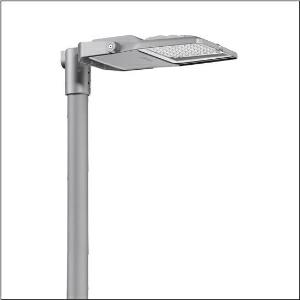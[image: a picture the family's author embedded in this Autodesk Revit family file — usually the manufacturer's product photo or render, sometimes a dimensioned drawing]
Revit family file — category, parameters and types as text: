
# Revit family: floodlight_fl_21_mini___pl52_5xa7776c4d3a_f656
name_source: partatom
category: Lighting Fixtures
units: mm (PartAtom-declared; Revit-internal decimal feet)

## family parameters
Cut with Voids When Loaded = No
Host = Face
Light Source = No
Part Type = Normal
Room Calculation Point = No
Round Connector Dimension = Use Diameter
Shared = No

## types (1)
- --- (1 x LED, 12700 lm, 89 W, 4000K)
    Apparent Load = 89 VA
    CIE Flux Codes = 26 60 98 100 100
    Color Rendering = 70
    Color Temperature = 4000K
    Default Elevation = 1800 mm
    Description = Floodlight FL 21 mini, floodlight, primary light control with lens, of PMMA, primary optical cover: protective disc, of toughened safety glass, transparent, light distribution: PL52, light emission: direct distribution, installation type: surface-mounted, LED, High Power LED, rated luminous flux: 12.700lm, luminous efficacy: 143lm/W, light colour: 740, colour temperature: 4000K, control gear: Smart Interface (Zhaga), control: pre-setting: logarithmic dimming characteristic, flexible luminous flux parameterisation, time-dependent luminous flux control, constant luminous flux control, overheat protection, with terminal, 6-pole, mains connection: 220..240V, AC, 50/60Hz, start of lifetime: 89W, end of service life: 94W, reduction: 43W, luminaire housing, of diecast aluminium, powder-coated, SITECO metallic grey (DB 702S), corrosivity category C5 mid according to DIN EN ISO 12944, suitable for swimming pools, chlorine-resistant, sealing non-destructively replaceable, please order mast flange separately, mast bracket, of steel, galvanised, powder-coated, SITECO metallic grey (DB 702S), Smart Interface below and above, protection rating (complete): IP66, insulation class (complete): insulation class II (safety insulation), certification: CE, ENEC, VDE, protection symbol: D, impact resistance: IK08, permissible operating ambient temperature: -40..+40°C, permissible operating ambient temperature for outdoor applications: -40..+50°C, standard: DIN EN 12944, LABS conformity tested according to VDMA 24364:2018-05, packaging unit: 1 piece

Light Distribution: PL52
    Height = 70 mm
    Lamp = 1 x LED
    Lamp Light Flux = 12700 lm
    Lamp Power = 89 W
    Lamp count = 1
    Length = 485 mm
    Luminous efficacy = 143 lm/W
    Manufacturer = Siteco
    ModVariant = No
    Model = 5XA7776C4D3A
    Mounting Place = Pole
    Mounting Type = Pole annexe
    Number of Poles = 1
    OnlyDefault = Yes
    Power Factor = 1
    Product Name = Floodlight FL 21 mini | PL52
    Product group = floodlight | pylon annexe
    ProductGroupID = 6201
    Protection Class = Protection class II
    Protection Degree = IP 66
    RLX_Detail_Level = 1
    RLX_Emergency_Light_Flux = 0 lm
    RLX_Emergency_Type = 0
    RLX_Emergency_Type_DB = No
    RlxData = <blob elided: 101245 chars, md5=00e5fea4>
    Socket = socket
    Standby Power = 0 W
    System Light Flux = 12700 lm
    System Power = 89 W
    Type Comments = factory setting: luminous flux: 100 % | dim-lin: 254 | 456 mA
    Type Image = l_1007125.jpg
    URL = http://relux.com
    VarID = @adj_039581
    Voltage = 0 V
    Weight = 0.00 kg
    Width = 337 mm

## geometry (parser evidence)
native form markers: Blend x4, Sweep x11
no freeform markers — native parametric forms only
